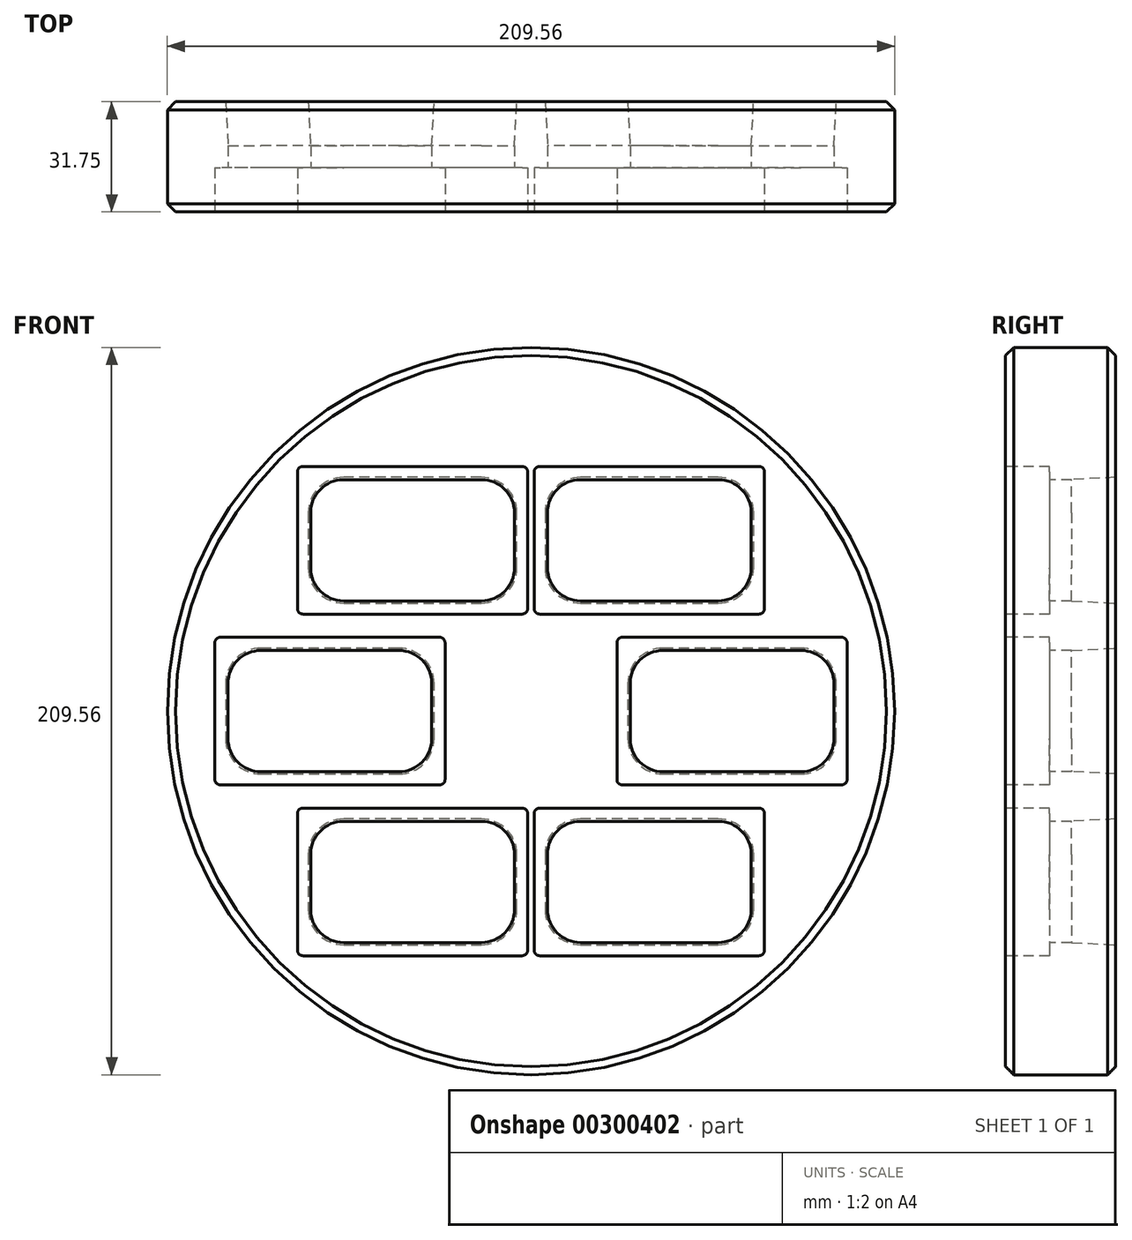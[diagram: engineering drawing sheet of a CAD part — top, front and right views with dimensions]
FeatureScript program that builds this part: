
annotation { "Feature Type Name" : "Feature", "Feature Type Description" : "" }
export const myFeature = defineFeature(function(context is Context, id is Id, definition is map)
    precondition{}
    {
        {
            var Q0;
            Q0=qCreatedBy(makeId("Front.planeOp"),FACE);
            var sketch = newSketch(context, id + "F0", { "sketchPlane" : qUnion([Q0])});
            skCircle(sketch, "E0", {"center": v(0, 0) * mm, "radius": 104.77 * mm});
            skSolve(sketch);
        }
        {
            var Q0;
            Q0 = qSketchRegion(id + "F0", true);
            extrude(context, id + "F1", {"entities" : qUnion([Q0]), "depth" : 31.75 * mm});
        }
        {
            var Q0;
            Q0=makeQuery(id+"F1.opExtrude","CAP_EDGE",EDGE,{"disambiguationData":[OSD([sQuery(id+"F0.wireOp",EDGE,"E0")])],"isStart":false});
            chamfer(context, id + "F2", {"entities" : qUnion([Q0]), "width" : 2.36 * mm, "tangentPropagation" : true});
        }
        {
            var Q0;
            Q0=makeQuery(id+"F1.opExtrude","CAP_EDGE",EDGE,{"disambiguationData":[OSD([sQuery(id+"F0.wireOp",EDGE,"E0")])],"isStart":true});
            chamfer(context, id + "F3", {"entities" : qUnion([Q0]), "width" : 2.36 * mm, "tangentPropagation" : true});
        }
        {
            var Q0;
            Q0=makeQuery(id+"F1.opExtrude","CAP_FACE",FACE,{"disambiguationData":[OSD([sQuery(id+"F0.wireOp",EDGE,"E0")])],"isStart":false});
            var sketch = newSketch(context, id + "F4", { "sketchPlane" : qUnion([Q0])});
            skLineSegment(sketch, "E1.bottom", {"start": v(-26.34, 21.27) * mm, "end": v(-89.53, 21.27) * mm});
            skLineSegment(sketch, "E1.top", {"start": v(-26.34, -21.27) * mm, "end": v(-89.53, -21.27) * mm});
            skLineSegment(sketch, "E1.left", {"start": v(-24.77, 19.7) * mm, "end": v(-24.77, -19.7) * mm});
            skLineSegment(sketch, "E1.right", {"start": v(-91.1, 19.7) * mm, "end": v(-91.1, -19.7) * mm});
            skPoint(sketch, "E1.middle", {"position": v(-57.94, 0) * mm});
            skLineSegment(sketch, "E2.bottom", {"start": v(89.54, 21.27) * mm, "end": v(26.34, 21.27) * mm});
            skLineSegment(sketch, "E2.top", {"start": v(89.54, -21.27) * mm, "end": v(26.34, -21.27) * mm});
            skLineSegment(sketch, "E2.left", {"start": v(91.1, 19.7) * mm, "end": v(91.1, -19.7) * mm});
            skLineSegment(sketch, "E2.right", {"start": v(24.77, 19.7) * mm, "end": v(24.77, -19.7) * mm});
            skPoint(sketch, "E2.middle", {"position": v(57.94, 0) * mm});
            skPoint(sketch, "E3.visualSharp", {"position": v(-91.1, 21.27) * mm});
            skArc(sketch, "E3.filletArc", {"start": v(-89.53, 21.27) * mm, "mid": v(-90.65, 20.81) * mm, "end": v(-91.1, 19.7) * mm});
            skPoint(sketch, "E4.visualSharp", {"position": v(-91.1, -21.27) * mm});
            skArc(sketch, "E4.filletArc", {"start": v(-91.1, -19.7) * mm, "mid": v(-90.65, -20.81) * mm, "end": v(-89.53, -21.27) * mm});
            skPoint(sketch, "E5.visualSharp", {"position": v(-24.77, -21.27) * mm});
            skArc(sketch, "E5.filletArc", {"start": v(-26.34, -21.27) * mm, "mid": v(-25.23, -20.81) * mm, "end": v(-24.77, -19.7) * mm});
            skPoint(sketch, "E6.visualSharp", {"position": v(-24.77, 21.27) * mm});
            skArc(sketch, "E6.filletArc", {"start": v(-24.77, 19.7) * mm, "mid": v(-25.23, 20.81) * mm, "end": v(-26.34, 21.27) * mm});
            skPoint(sketch, "E7.visualSharp", {"position": v(24.77, 21.27) * mm});
            skArc(sketch, "E7.filletArc", {"start": v(26.34, 21.27) * mm, "mid": v(25.23, 20.81) * mm, "end": v(24.77, 19.7) * mm});
            skPoint(sketch, "E8.visualSharp", {"position": v(24.77, -21.27) * mm});
            skArc(sketch, "E8.filletArc", {"start": v(24.77, -19.7) * mm, "mid": v(25.23, -20.81) * mm, "end": v(26.34, -21.27) * mm});
            skPoint(sketch, "E9.visualSharp", {"position": v(91.1, -21.27) * mm});
            skArc(sketch, "E9.filletArc", {"start": v(89.54, -21.27) * mm, "mid": v(90.65, -20.81) * mm, "end": v(91.1, -19.7) * mm});
            skPoint(sketch, "E10.visualSharp", {"position": v(91.1, 21.27) * mm});
            skArc(sketch, "E10.filletArc", {"start": v(91.1, 19.7) * mm, "mid": v(90.65, 20.81) * mm, "end": v(89.54, 21.27) * mm});
            skLineSegment(sketch, "E11.bottom", {"start": v(-2.53, 70.49) * mm, "end": v(-65.72, 70.49) * mm});
            skLineSegment(sketch, "E11.top", {"start": v(-2.53, 27.94) * mm, "end": v(-65.72, 27.94) * mm});
            skLineSegment(sketch, "E11.left", {"start": v(-0.95, 68.91) * mm, "end": v(-0.95, 29.51) * mm});
            skLineSegment(sketch, "E11.right", {"start": v(-67.3, 68.91) * mm, "end": v(-67.3, 29.51) * mm});
            skPoint(sketch, "E11.middle", {"position": v(-34.12, 49.21) * mm});
            skPoint(sketch, "E12.visualSharp", {"position": v(-67.3, 70.49) * mm});
            skArc(sketch, "E12.filletArc", {"start": v(-65.72, 70.49) * mm, "mid": v(-66.84, 70.02) * mm, "end": v(-67.3, 68.91) * mm});
            skPoint(sketch, "E13.visualSharp", {"position": v(-67.3, 27.94) * mm});
            skArc(sketch, "E13.filletArc", {"start": v(-67.3, 29.51) * mm, "mid": v(-66.84, 28.4) * mm, "end": v(-65.72, 27.94) * mm});
            skPoint(sketch, "E14.visualSharp", {"position": v(-0.95, 27.94) * mm});
            skArc(sketch, "E14.filletArc", {"start": v(-2.53, 27.94) * mm, "mid": v(-1.41, 28.4) * mm, "end": v(-0.95, 29.51) * mm});
            skPoint(sketch, "E15.visualSharp", {"position": v(-0.95, 70.49) * mm});
            skArc(sketch, "E15.filletArc", {"start": v(-0.95, 68.91) * mm, "mid": v(-1.41, 70.02) * mm, "end": v(-2.53, 70.49) * mm});
            skLineSegment(sketch, "E16.bottom", {"start": v(2.51, 70.49) * mm, "end": v(65.7, 70.49) * mm});
            skLineSegment(sketch, "E16.top", {"start": v(2.51, 27.94) * mm, "end": v(65.7, 27.94) * mm});
            skLineSegment(sketch, "E16.left", {"start": v(0.94, 68.91) * mm, "end": v(0.94, 29.51) * mm});
            skLineSegment(sketch, "E16.right", {"start": v(67.28, 68.91) * mm, "end": v(67.28, 29.51) * mm});
            skPoint(sketch, "E16.middle", {"position": v(34.11, 49.21) * mm});
            skPoint(sketch, "E17.visualSharp", {"position": v(0.94, 70.49) * mm});
            skArc(sketch, "E17.filletArc", {"start": v(2.51, 70.49) * mm, "mid": v(1.4, 70.02) * mm, "end": v(0.94, 68.91) * mm});
            skPoint(sketch, "E18.visualSharp", {"position": v(0.94, 27.94) * mm});
            skArc(sketch, "E18.filletArc", {"start": v(0.94, 29.51) * mm, "mid": v(1.4, 28.4) * mm, "end": v(2.51, 27.94) * mm});
            skPoint(sketch, "E19.visualSharp", {"position": v(67.28, 27.94) * mm});
            skArc(sketch, "E19.filletArc", {"start": v(65.7, 27.94) * mm, "mid": v(66.82, 28.4) * mm, "end": v(67.28, 29.51) * mm});
            skPoint(sketch, "E20.visualSharp", {"position": v(67.28, 70.49) * mm});
            skArc(sketch, "E20.filletArc", {"start": v(67.28, 68.91) * mm, "mid": v(66.82, 70.02) * mm, "end": v(65.7, 70.49) * mm});
            skLineSegment(sketch, "E21.bottom", {"start": v(-2.53, -27.94) * mm, "end": v(-65.72, -27.94) * mm});
            skLineSegment(sketch, "E21.top", {"start": v(-2.53, -70.48) * mm, "end": v(-65.72, -70.48) * mm});
            skLineSegment(sketch, "E21.left", {"start": v(-0.95, -29.51) * mm, "end": v(-0.95, -68.91) * mm});
            skLineSegment(sketch, "E21.right", {"start": v(-67.3, -29.51) * mm, "end": v(-67.3, -68.91) * mm});
            skPoint(sketch, "E21.middle", {"position": v(-34.12, -49.21) * mm});
            skPoint(sketch, "E21.middle.positionSnap0", {"position": v(-34.12, 27.94) * mm});
            skPoint(sketch, "E21.centerSnap0", {"position": v(-34.12, 27.94) * mm});
            skLineSegment(sketch, "E22.bottom", {"start": v(2.51, -27.94) * mm, "end": v(65.7, -27.94) * mm});
            skLineSegment(sketch, "E22.top", {"start": v(2.51, -70.48) * mm, "end": v(65.7, -70.48) * mm});
            skLineSegment(sketch, "E22.left", {"start": v(0.94, -29.51) * mm, "end": v(0.94, -68.91) * mm});
            skLineSegment(sketch, "E22.right", {"start": v(67.28, -29.51) * mm, "end": v(67.28, -68.91) * mm});
            skPoint(sketch, "E22.middle", {"position": v(34.11, -49.21) * mm});
            skPoint(sketch, "E22.middle.positionSnap0", {"position": v(-0.95, -49.21) * mm});
            skPoint(sketch, "E22.middle.positionSnap1", {"position": v(34.11, 27.94) * mm});
            skPoint(sketch, "E22.centerSnap0", {"position": v(-0.95, -49.21) * mm});
            skPoint(sketch, "E22.centerSnap1", {"position": v(34.11, 27.94) * mm});
            skPoint(sketch, "E23.visualSharp", {"position": v(-67.3, -27.94) * mm});
            skArc(sketch, "E23.filletArc", {"start": v(-65.72, -27.94) * mm, "mid": v(-66.84, -28.4) * mm, "end": v(-67.3, -29.51) * mm});
            skPoint(sketch, "E24.visualSharp", {"position": v(-67.3, -70.48) * mm});
            skArc(sketch, "E24.filletArc", {"start": v(-67.3, -68.91) * mm, "mid": v(-66.84, -70.02) * mm, "end": v(-65.72, -70.48) * mm});
            skPoint(sketch, "E25.visualSharp", {"position": v(-0.95, -70.48) * mm});
            skArc(sketch, "E25.filletArc", {"start": v(-2.53, -70.48) * mm, "mid": v(-1.41, -70.02) * mm, "end": v(-0.95, -68.91) * mm});
            skPoint(sketch, "E26.visualSharp", {"position": v(0.94, -70.48) * mm});
            skArc(sketch, "E26.filletArc", {"start": v(0.94, -68.91) * mm, "mid": v(1.4, -70.02) * mm, "end": v(2.51, -70.48) * mm});
            skPoint(sketch, "E27.visualSharp", {"position": v(-0.95, -27.94) * mm});
            skArc(sketch, "E27.filletArc", {"start": v(-0.95, -29.51) * mm, "mid": v(-1.41, -28.4) * mm, "end": v(-2.53, -27.94) * mm});
            skPoint(sketch, "E28.visualSharp", {"position": v(0.94, -27.94) * mm});
            skArc(sketch, "E28.filletArc", {"start": v(2.51, -27.94) * mm, "mid": v(1.4, -28.4) * mm, "end": v(0.94, -29.51) * mm});
            skPoint(sketch, "E29.visualSharp", {"position": v(67.28, -27.94) * mm});
            skArc(sketch, "E29.filletArc", {"start": v(67.28, -29.51) * mm, "mid": v(66.82, -28.4) * mm, "end": v(65.7, -27.94) * mm});
            skPoint(sketch, "E30.visualSharp", {"position": v(67.28, -70.48) * mm});
            skArc(sketch, "E30.filletArc", {"start": v(65.7, -70.48) * mm, "mid": v(66.82, -70.02) * mm, "end": v(67.28, -68.91) * mm});
            skSolve(sketch);
        }
        {
            var Q0;
            Q0 = qSketchRegion(id + "F4", true);
            extrude(context, id + "F5", {"entities" : qUnion([Q0]), "operationType" : NewBodyOperationType.REMOVE, "oppositeDirection" : true, "depth" : 12.7 * mm});
        }
        {
            var Q0;
            Q0=makeQuery(id+"F5.boolean.opBoolean","COPY",FACE,{"derivedFrom":makeQuery(id+"F5.opExtrude","CAP_FACE",FACE,{"disambiguationData":[OSD([sQuery(id+"F4.wireOp",EDGE,"E11.bottom"),sQuery(id+"F4.wireOp",EDGE,"E11.top"),sQuery(id+"F4.wireOp",EDGE,"E11.left"),sQuery(id+"F4.wireOp",EDGE,"E11.right"),sQuery(id+"F4.wireOp",EDGE,"E12.filletArc"),sQuery(id+"F4.wireOp",EDGE,"E13.filletArc"),sQuery(id+"F4.wireOp",EDGE,"E14.filletArc"),sQuery(id+"F4.wireOp",EDGE,"E15.filletArc")])],"isStart":false})});
            var sketch = newSketch(context, id + "F6", { "sketchPlane" : qUnion([Q0])});
            skLineSegment(sketch, "E31.bottom", {"start": v(-14.29, 66.68) * mm, "end": v(-53.96, 66.68) * mm});
            skLineSegment(sketch, "E31.top", {"start": v(-14.29, 31.75) * mm, "end": v(-53.96, 31.75) * mm});
            skLineSegment(sketch, "E31.left", {"start": v(-4.76, 57.15) * mm, "end": v(-4.76, 41.28) * mm});
            skLineSegment(sketch, "E31.right", {"start": v(-63.49, 57.15) * mm, "end": v(-63.49, 41.28) * mm});
            skPoint(sketch, "E31.middle", {"position": v(-34.12, 49.21) * mm});
            skPoint(sketch, "E31.middle.positionSnap0", {"position": v(-34.12, 27.94) * mm});
            skPoint(sketch, "E31.middle.positionSnap1", {"position": v(-0.95, 49.21) * mm});
            skPoint(sketch, "E31.centerSnap0", {"position": v(-34.12, 27.94) * mm});
            skPoint(sketch, "E31.centerSnap1", {"position": v(-0.95, 49.21) * mm});
            skPoint(sketch, "E32.visualSharp", {"position": v(-63.49, 66.68) * mm});
            skArc(sketch, "E32.filletArc", {"start": v(-53.96, 66.68) * mm, "mid": v(-60.7, 63.89) * mm, "end": v(-63.49, 57.15) * mm});
            skPoint(sketch, "E33.visualSharp", {"position": v(-63.49, 31.75) * mm});
            skArc(sketch, "E33.filletArc", {"start": v(-63.49, 41.28) * mm, "mid": v(-60.7, 34.54) * mm, "end": v(-53.96, 31.75) * mm});
            skPoint(sketch, "E34.visualSharp", {"position": v(-4.76, 31.75) * mm});
            skArc(sketch, "E34.filletArc", {"start": v(-14.29, 31.75) * mm, "mid": v(-7.55, 34.54) * mm, "end": v(-4.76, 41.28) * mm});
            skPoint(sketch, "E35.visualSharp", {"position": v(-4.76, 66.68) * mm});
            skArc(sketch, "E35.filletArc", {"start": v(-4.76, 57.15) * mm, "mid": v(-7.55, 63.89) * mm, "end": v(-14.29, 66.68) * mm});
            skArc(sketch, "E36.MirrorCS", {"start": v(63.49, 41.28) * mm, "mid": v(60.7, 34.54) * mm, "end": v(53.96, 31.75) * mm});
            skLineSegment(sketch, "E37.MirrorCS", {"start": v(14.29, 31.75) * mm, "end": v(53.96, 31.75) * mm});
            skArc(sketch, "E38.MirrorCS", {"start": v(14.29, 31.75) * mm, "mid": v(7.55, 34.54) * mm, "end": v(4.76, 41.28) * mm});
            skLineSegment(sketch, "E39.MirrorCS", {"start": v(4.76, 57.15) * mm, "end": v(4.76, 41.28) * mm});
            skArc(sketch, "E40.MirrorCS", {"start": v(4.76, 57.15) * mm, "mid": v(7.55, 63.89) * mm, "end": v(14.29, 66.68) * mm});
            skLineSegment(sketch, "E41.MirrorCS", {"start": v(63.49, 57.15) * mm, "end": v(63.49, 41.28) * mm});
            skLineSegment(sketch, "E42.MirrorCS", {"start": v(14.29, 66.68) * mm, "end": v(53.96, 66.68) * mm});
            skArc(sketch, "E43.MirrorCS", {"start": v(53.96, 66.68) * mm, "mid": v(60.7, 63.89) * mm, "end": v(63.49, 57.15) * mm});
            skLineSegment(sketch, "E44.MirrorCS", {"start": v(14.29, -66.68) * mm, "end": v(53.96, -66.68) * mm});
            skArc(sketch, "E45.MirrorCS", {"start": v(53.96, -66.68) * mm, "mid": v(60.7, -63.89) * mm, "end": v(63.49, -57.15) * mm});
            skLineSegment(sketch, "E46.MirrorCS", {"start": v(63.49, -57.15) * mm, "end": v(63.49, -41.28) * mm});
            skArc(sketch, "E47.MirrorCS", {"start": v(63.49, -41.28) * mm, "mid": v(60.7, -34.54) * mm, "end": v(53.96, -31.75) * mm});
            skLineSegment(sketch, "E48.MirrorCS", {"start": v(14.29, -31.75) * mm, "end": v(53.96, -31.75) * mm});
            skArc(sketch, "E49.MirrorCS", {"start": v(14.29, -31.75) * mm, "mid": v(7.55, -34.54) * mm, "end": v(4.76, -41.28) * mm});
            skLineSegment(sketch, "E50.MirrorCS", {"start": v(4.76, -57.15) * mm, "end": v(4.76, -41.28) * mm});
            skArc(sketch, "E51.MirrorCS", {"start": v(4.76, -57.15) * mm, "mid": v(7.55, -63.89) * mm, "end": v(14.29, -66.68) * mm});
            skArc(sketch, "E52.MirrorCS", {"start": v(-53.96, -66.68) * mm, "mid": v(-60.7, -63.89) * mm, "end": v(-63.49, -57.15) * mm});
            skLineSegment(sketch, "E53.MirrorCS", {"start": v(-63.49, -57.15) * mm, "end": v(-63.49, -41.28) * mm});
            skArc(sketch, "E54.MirrorCS", {"start": v(-63.49, -41.28) * mm, "mid": v(-60.7, -34.54) * mm, "end": v(-53.96, -31.75) * mm});
            skLineSegment(sketch, "E55.MirrorCS", {"start": v(-14.29, -31.75) * mm, "end": v(-53.96, -31.75) * mm});
            skArc(sketch, "E56.MirrorCS", {"start": v(-14.29, -31.75) * mm, "mid": v(-7.55, -34.54) * mm, "end": v(-4.76, -41.28) * mm});
            skLineSegment(sketch, "E57.MirrorCS", {"start": v(-14.29, -66.68) * mm, "end": v(-53.96, -66.68) * mm});
            skLineSegment(sketch, "E58.MirrorCS", {"start": v(-4.76, -57.15) * mm, "end": v(-4.76, -41.28) * mm});
            skArc(sketch, "E59.MirrorCS", {"start": v(-4.76, -57.15) * mm, "mid": v(-7.55, -63.89) * mm, "end": v(-14.29, -66.68) * mm});
            skLineSegment(sketch, "E60.bottom", {"start": v(-38.1, 17.46) * mm, "end": v(-77.77, 17.46) * mm});
            skLineSegment(sketch, "E60.top", {"start": v(-38.1, -17.46) * mm, "end": v(-77.77, -17.46) * mm});
            skLineSegment(sketch, "E60.left", {"start": v(-28.58, 7.94) * mm, "end": v(-28.58, -7.94) * mm});
            skLineSegment(sketch, "E60.right", {"start": v(-87.3, 7.94) * mm, "end": v(-87.3, -7.94) * mm});
            skPoint(sketch, "E60.middle", {"position": v(-57.94, 0) * mm});
            skPoint(sketch, "E61.visualSharp", {"position": v(-87.3, 17.46) * mm});
            skArc(sketch, "E61.filletArc", {"start": v(-77.77, 17.46) * mm, "mid": v(-84.5, 14.67) * mm, "end": v(-87.3, 7.94) * mm});
            skPoint(sketch, "E62.visualSharp", {"position": v(-87.3, -17.46) * mm});
            skArc(sketch, "E62.filletArc", {"start": v(-87.3, -7.94) * mm, "mid": v(-84.5, -14.67) * mm, "end": v(-77.77, -17.46) * mm});
            skPoint(sketch, "E63.visualSharp", {"position": v(-28.58, -17.46) * mm});
            skArc(sketch, "E63.filletArc", {"start": v(-38.1, -17.46) * mm, "mid": v(-31.36, -14.67) * mm, "end": v(-28.58, -7.94) * mm});
            skPoint(sketch, "E64.visualSharp", {"position": v(-28.58, 17.46) * mm});
            skArc(sketch, "E64.filletArc", {"start": v(-28.58, 7.94) * mm, "mid": v(-31.36, 14.67) * mm, "end": v(-38.1, 17.46) * mm});
            skLineSegment(sketch, "E65.MirrorCS", {"start": v(38.1, 17.46) * mm, "end": v(77.77, 17.46) * mm});
            skArc(sketch, "E66.MirrorCS", {"start": v(28.58, 7.94) * mm, "mid": v(31.36, 14.67) * mm, "end": v(38.1, 17.46) * mm});
            skLineSegment(sketch, "E67.MirrorCS", {"start": v(28.58, 7.94) * mm, "end": v(28.58, -7.94) * mm});
            skArc(sketch, "E68.MirrorCS", {"start": v(38.1, -17.46) * mm, "mid": v(31.36, -14.67) * mm, "end": v(28.58, -7.94) * mm});
            skLineSegment(sketch, "E69.MirrorCS", {"start": v(87.3, 7.94) * mm, "end": v(87.3, -7.94) * mm});
            skLineSegment(sketch, "E70.MirrorCS", {"start": v(38.1, -17.46) * mm, "end": v(77.77, -17.46) * mm});
            skArc(sketch, "E71.MirrorCS", {"start": v(87.3, -7.94) * mm, "mid": v(84.5, -14.67) * mm, "end": v(77.77, -17.46) * mm});
            skArc(sketch, "E72.MirrorCS", {"start": v(77.77, 17.46) * mm, "mid": v(84.5, 14.67) * mm, "end": v(87.3, 7.94) * mm});
            skSolve(sketch);
        }
        {
            var Q0;
            Q0 = qSketchRegion(id + "F6", true);
            extrude(context, id + "F7", {"entities" : qUnion([Q0]), "operationType" : NewBodyOperationType.REMOVE, "endBound" : BoundingType.THROUGH_ALL, "oppositeDirection" : true, "depth" : 25.4 * mm});
        }
        {
            var Q0;
            Q0=makeQuery(id+"F7.boolean.opBoolean","INTERSECT",EDGE,{"derivedFrom":[makeQuery(id+"F1.opExtrude","CAP_FACE",FACE,{"disambiguationData":[OSD([sQuery(id+"F0.wireOp",EDGE,"E0")])],"isStart":true}),makeQuery(id+"F7.opExtrude","SWEPT_FACE",FACE,{"disambiguationData":[OSD([sQuery(id+"F6.wireOp",EDGE,"E42.MirrorCS")])]})]});
            var Q1;
            Q1=makeQuery(id+"F7.boolean.opBoolean","INTERSECT",EDGE,{"derivedFrom":[makeQuery(id+"F1.opExtrude","CAP_FACE",FACE,{"disambiguationData":[OSD([sQuery(id+"F0.wireOp",EDGE,"E0")])],"isStart":true}),makeQuery(id+"F7.opExtrude","SWEPT_FACE",FACE,{"disambiguationData":[OSD([sQuery(id+"F6.wireOp",EDGE,"E31.bottom")])]})]});
            var Q2;
            Q2=makeQuery(id+"F7.boolean.opBoolean","INTERSECT",EDGE,{"derivedFrom":[makeQuery(id+"F1.opExtrude","CAP_FACE",FACE,{"disambiguationData":[OSD([sQuery(id+"F0.wireOp",EDGE,"E0")])],"isStart":true}),makeQuery(id+"F7.opExtrude","SWEPT_FACE",FACE,{"disambiguationData":[OSD([sQuery(id+"F6.wireOp",EDGE,"E60.bottom")])]})]});
            var Q3;
            Q3=makeQuery(id+"F7.boolean.opBoolean","INTERSECT",EDGE,{"derivedFrom":[makeQuery(id+"F1.opExtrude","CAP_FACE",FACE,{"disambiguationData":[OSD([sQuery(id+"F0.wireOp",EDGE,"E0")])],"isStart":true}),makeQuery(id+"F7.opExtrude","SWEPT_FACE",FACE,{"disambiguationData":[OSD([sQuery(id+"F6.wireOp",EDGE,"E65.MirrorCS")])]})]});
            var Q4;
            Q4=makeQuery(id+"F7.boolean.opBoolean","INTERSECT",EDGE,{"derivedFrom":[makeQuery(id+"F1.opExtrude","CAP_FACE",FACE,{"disambiguationData":[OSD([sQuery(id+"F0.wireOp",EDGE,"E0")])],"isStart":true}),makeQuery(id+"F7.opExtrude","SWEPT_FACE",FACE,{"disambiguationData":[OSD([sQuery(id+"F6.wireOp",EDGE,"E48.MirrorCS")])]})]});
            var Q5;
            Q5=makeQuery(id+"F7.boolean.opBoolean","INTERSECT",EDGE,{"derivedFrom":[makeQuery(id+"F1.opExtrude","CAP_FACE",FACE,{"disambiguationData":[OSD([sQuery(id+"F0.wireOp",EDGE,"E0")])],"isStart":true}),makeQuery(id+"F7.opExtrude","SWEPT_FACE",FACE,{"disambiguationData":[OSD([sQuery(id+"F6.wireOp",EDGE,"E55.MirrorCS")])]})]});
            chamfer(context, id + "F8", {"entities" : qUnion([Q0, Q1, Q2, Q3, Q4, Q5]), "chamferType" : ChamferType.OFFSET_ANGLE, "width" : 12.7 * mm, "oppositeDirection" : false, "angle" : 3 * degree, "tangentPropagation" : true});
        }
    });
